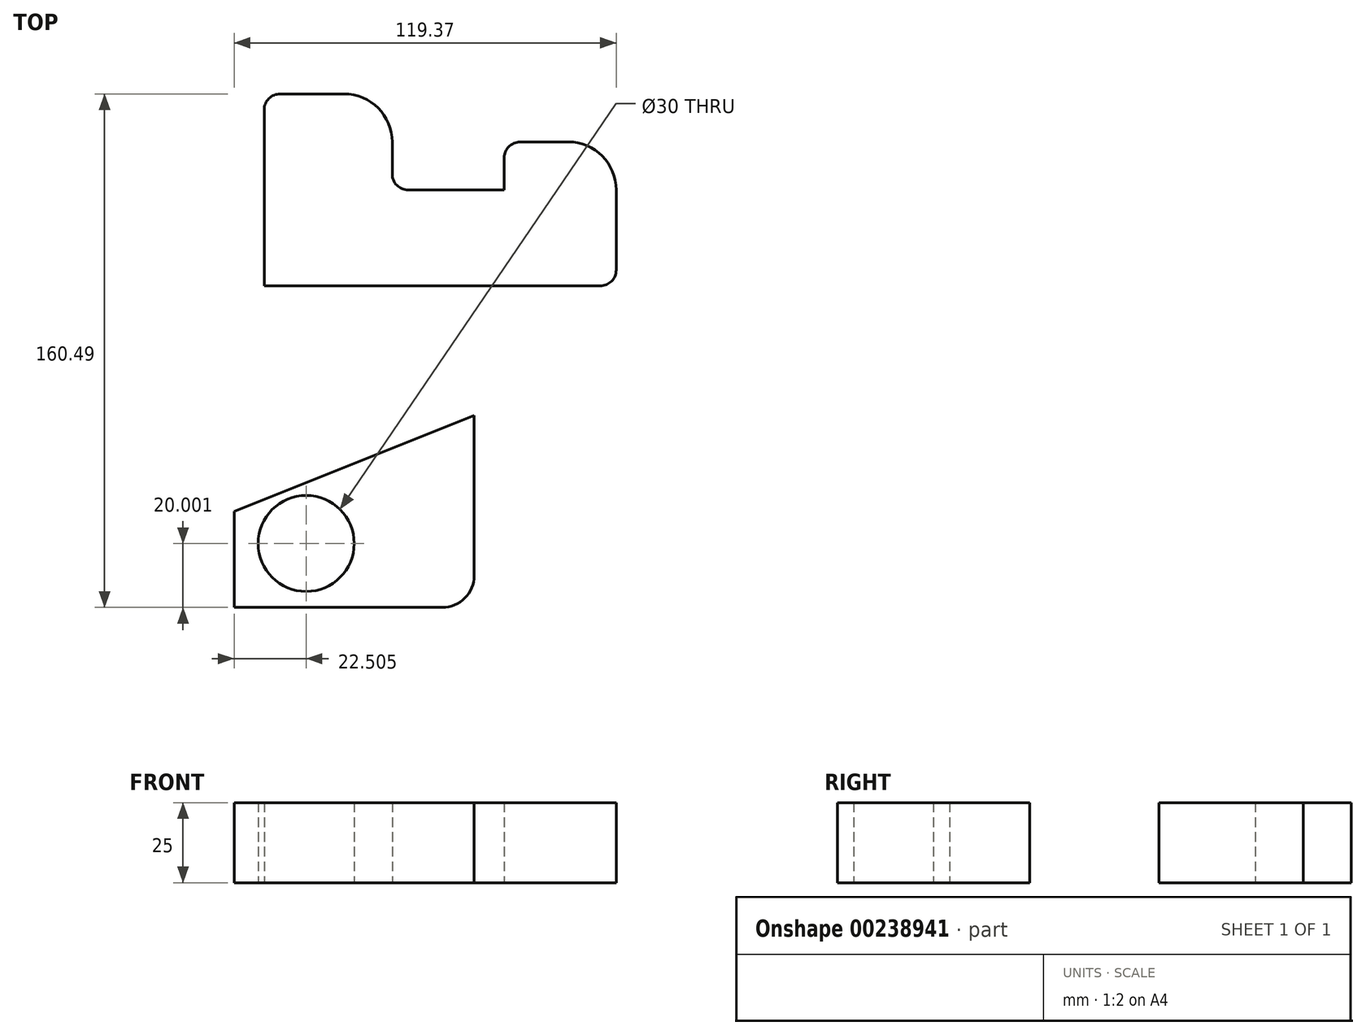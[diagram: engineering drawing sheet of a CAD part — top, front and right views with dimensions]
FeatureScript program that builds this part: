
annotation { "Feature Type Name" : "Feature", "Feature Type Description" : "" }
export const myFeature = defineFeature(function(context is Context, id is Id, definition is map)
    precondition{}
    {
        {
            var Q0;
            Q0=qCreatedBy(makeId("Top.planeOp"),FACE);
            var sketch = newSketch(context, id + "F0", { "sketchPlane" : qUnion([Q0])});
            skLineSegment(sketch, "E0", {"start": v(-68.27, -37.35) * mm, "end": v(36.73, -37.35) * mm});
            skLineSegment(sketch, "E1", {"start": v(-68.27, -37.35) * mm, "end": v(-68.27, 17.65) * mm});
            skLineSegment(sketch, "E2", {"start": v(-63.27, 22.65) * mm, "end": v(-43.27, 22.65) * mm});
            skLineSegment(sketch, "E3", {"start": v(-28.27, 7.65) * mm, "end": v(-28.27, -2.35) * mm});
            skLineSegment(sketch, "E4", {"start": v(-23.27, -7.35) * mm, "end": v(6.73, -7.35) * mm});
            skLineSegment(sketch, "E5", {"start": v(6.73, -7.35) * mm, "end": v(6.73, 2.65) * mm});
            skLineSegment(sketch, "E6", {"start": v(11.73, 7.65) * mm, "end": v(26.73, 7.65) * mm});
            skLineSegment(sketch, "E7", {"start": v(41.73, -7.35) * mm, "end": v(41.73, -32.35) * mm});
            skPoint(sketch, "E8.visualSharp", {"position": v(-68.27, 22.65) * mm});
            skArc(sketch, "E8.filletArc", {"start": v(-63.27, 22.65) * mm, "mid": v(-66.8, 21.18) * mm, "end": v(-68.27, 17.65) * mm});
            skPoint(sketch, "E9.visualSharp", {"position": v(-28.27, 22.65) * mm});
            skArc(sketch, "E9.filletArc", {"start": v(-28.27, 7.65) * mm, "mid": v(-32.66, 18.25) * mm, "end": v(-43.27, 22.65) * mm});
            skPoint(sketch, "E10.visualSharp", {"position": v(-28.27, -7.35) * mm});
            skArc(sketch, "E10.filletArc", {"start": v(-28.27, -2.35) * mm, "mid": v(-26.8, -5.89) * mm, "end": v(-23.27, -7.35) * mm});
            skPoint(sketch, "E11.visualSharp", {"position": v(6.73, 7.65) * mm});
            skArc(sketch, "E11.filletArc", {"start": v(11.73, 7.65) * mm, "mid": v(8.2, 6.18) * mm, "end": v(6.73, 2.65) * mm});
            skPoint(sketch, "E12.visualSharp", {"position": v(41.73, 7.65) * mm});
            skArc(sketch, "E12.filletArc", {"start": v(41.73, -7.35) * mm, "mid": v(37.34, 3.25) * mm, "end": v(26.73, 7.65) * mm});
            skPoint(sketch, "E13.visualSharp", {"position": v(41.73, -37.35) * mm});
            skArc(sketch, "E13.filletArc", {"start": v(36.73, -37.35) * mm, "mid": v(40.27, -35.89) * mm, "end": v(41.73, -32.35) * mm});
            skLineSegment(sketch, "E14", {"start": v(-77.64, -137.84) * mm, "end": v(-12.64, -137.84) * mm});
            skLineSegment(sketch, "E15", {"start": v(-2.64, -127.84) * mm, "end": v(-2.64, -77.84) * mm});
            skLineSegment(sketch, "E16", {"start": v(-77.64, -137.84) * mm, "end": v(-77.64, -107.84) * mm});
            skLineSegment(sketch, "E17", {"start": v(-77.64, -107.84) * mm, "end": v(-2.64, -77.84) * mm});
            skCircle(sketch, "E18", {"center": v(-55.14, -117.84) * mm, "radius": 15 * mm});
            skPoint(sketch, "E19.visualSharp", {"position": v(-2.64, -137.84) * mm});
            skArc(sketch, "E19.filletArc", {"start": v(-12.64, -137.84) * mm, "mid": v(-5.56, -134.9) * mm, "end": v(-2.64, -127.84) * mm});
            skSolve(sketch);
        }
        {
            var Q0;
            Q0=makeQuery(id+"F0.imprint","IMPRINT",FACE,{"disambiguationData":[TD([[makeQuery(id+"F0.imprint","IMPRINT",EDGE,{"derivedFrom":sQuery(id+"F0.wireOp",EDGE,"E0")}),1.0]])]});
            extrude(context, id + "F1", {"entities" : qUnion([Q0]), "depth" : 25 * mm});
        }
        {
            var Q0;
            Q0=makeQuery(id+"F0.imprint","IMPRINT",FACE,{"disambiguationData":[TD([[makeQuery(id+"F0.imprint","IMPRINT",EDGE,{"derivedFrom":sQuery(id+"F0.wireOp",EDGE,"E14")}),1.0]])]});
            extrude(context, id + "F2", {"entities" : qUnion([Q0]), "depth" : 25 * mm});
        }
    });
